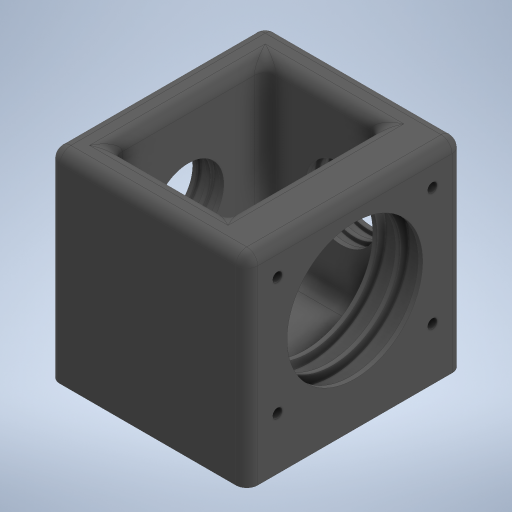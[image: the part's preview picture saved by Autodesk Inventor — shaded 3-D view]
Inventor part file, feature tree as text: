
AUTODESK INVENTOR PART (.ipt)
format: ipt  version: 2024.2 (Build 282272000, 272)  size: 567,296 bytes
history: native  units: in
note: dims shown in document units (in); Inventor stores cm internally (conversion verified against a paired STEP export)
features: sketch x23, extrude x22, fillet x5
ambient origin geometry x8: Origin, YZ Plane, XZ Plane, XY Plane, X Axis, Y Axis, Z Axis, Center Point
bodies: Solid1 (feature_tree)
feature tree (50):
  extrude  "Extrusion1"  Depth=2.472in
  extrude  "Extrusion2"  Depth=1.236in
  extrude  "Extrusion3"  Depth=1.552in
  extrude  "Extrusion4"  Depth=1.752in
  extrude  "Extrusion5"  Depth=0.05in TaperAngle=0.0deg
  extrude  "Extrusion6"  Depth=0.05in TaperAngle=0.0deg
  extrude  "Extrusion7"  Depth=1.0236in
  extrude  "Extrusion8"  Depth=0.813in
  extrude  "Extrusion9"  Depth=0.906in
  extrude  "Extrusion10"  Depth=0.05in TaperAngle=0.0deg
  extrude  "Extrusion11"  Depth=0.05in TaperAngle=0.0deg
  extrude  "Extrusion12"  Depth=1.0236in
  extrude  "Extrusion13"  Depth=0.05in TaperAngle=0.0deg
  extrude  "Extrusion14"  Depth=0.103in TaperAngle=0.0deg
  extrude  "Extrusion15"  Depth=0.906in
  extrude  "Extrusion16"  Depth=0.05in TaperAngle=0.0deg
  extrude  "Extrusion17"  Depth=0.356in
  sketch  "Sketch18"  dims[d50=0.356in d51=0.356in]
  extrude  "Extrusion18"  Depth=0.356in
  extrude  "Extrusion19"  Depth=0.5in
  extrude  "Extrusion20"  Depth=0.7in
  extrude  "Extrusion21"  Depth=0.7in
  extrude  "Extrusion22"  Depth=0.5in
  fillet  "Fillet1"  Radius=0.5in
  fillet  "Face Fillet1"
  fillet  "Face Fillet2"
  fillet  "Face Fillet3"
  fillet  "Face Fillet4"
  sketch  "Sketch1"  dims[d0=2.2609in d1=2.472in]
  sketch  "Sketch2"  dims[d2=2.0472in d3=0.0in d4=1.236in]
  sketch  "Sketch3"  dims[d5=1.0236in d6=1.552in]
  sketch  "Sketch4"  dims[d7=0.05in d8=0.0in d9=1.752in]
  sketch  "Sketch5"  dims[d10=0.21in d11=0.0in d12=0.05in d13=0.0in]
  sketch  "Sketch6"  dims[d14=0.21in d15=0.0in d16=0.05in d17=0.0in]
  sketch  "Sketch7"  dims[d18=0.57in d19=1.0236in]
  sketch  "Sketch8"  dims[d20=0.4647in d21=0.813in]
  sketch  "Sketch9"  dims[d22=0.05in d23=0.0in d24=0.906in]
  sketch  "Sketch10"  dims[d25=0.103in d26=0.0in d27=0.05in d28=0.0in]
  sketch  "Sketch11"  dims[d29=0.103in d30=0.0in d31=0.05in d32=0.0in]
  sketch  "Sketch12"  dims[d33=1.236in d34=1.0236in]
  sketch  "Sketch13"  dims[d35=0.813in d36=0.05in d37=0.0in]
  sketch  "Sketch14"  dims[d38=0.906in d39=0.103in d40=0.0in]
  sketch  "Sketch15"  dims[d41=0.05in d42=0.0in d43=0.906in]
  sketch  "Sketch16"  dims[d44=0.103in d45=0.0in d46=0.05in d47=0.0in]
  sketch  "Sketch17"  dims[d48=0.57in d49=0.356in]
  sketch  "Sketch19"  dims[d52=2.0079in d53=0.0in d54=0.5in]
  sketch  "Sketch20"  dims[d55=0.5in d56=0.7in]
  sketch  "Sketch21"  dims[d57=0.5in d58=0.7in]
  sketch  "Sketch22"  dims[d59=0.5in d60=0.5in d61=0.5in]
  sketch  "Sketch23"  dims[d62=0.1061in d63=0.1061in d64=0.1061in d65=0.1061in d66=0.25in d67=0.0in d68=0.705in d69=0.5in d70=0.705in d71=0.5in d72=0.705in d73=0.5in d74=0.705in d75=0.5in d76=0.1061in d77=0.1061in d78=0.1061in d79=0.1061in d80=0.25in d81=0.0in d82=0.35in d83=0.35in d84=0.35in d85=0.35in d86=0.35in d87=0.35in d88=0.35in d89=0.35in d90=0.1061in d91=0.1061in d92=0.1061in d93=0.1061in d94=0.25in d95=0.0in d96=0.25in d97=0.0in d98=1.1305in d99=1.236in d100=0.1571in d101=0.25in d102=0.0in d103=0.125in d104=0.125in d105=0.125in d106=0.125in d107=0.125in]
